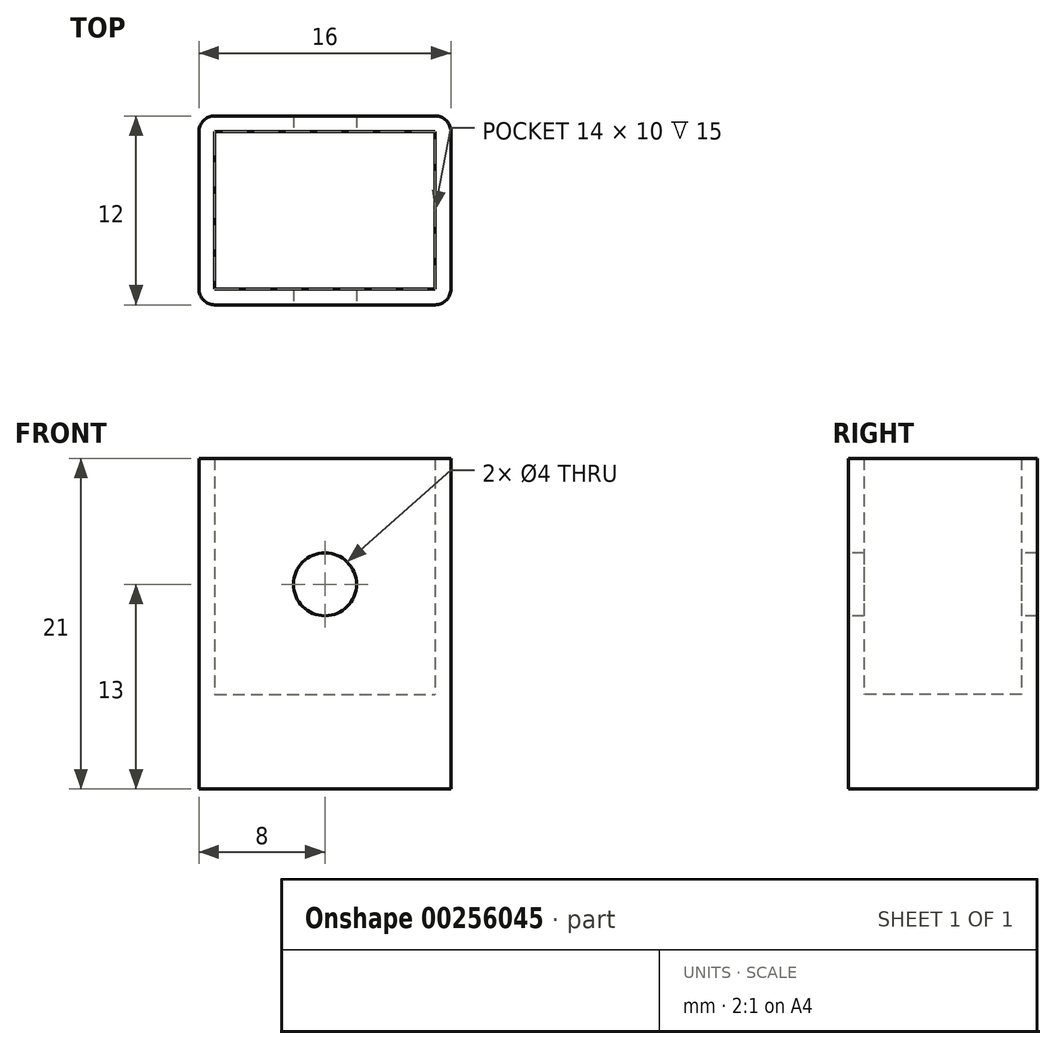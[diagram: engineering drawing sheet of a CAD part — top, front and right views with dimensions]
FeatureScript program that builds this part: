
annotation { "Feature Type Name" : "Feature", "Feature Type Description" : "" }
export const myFeature = defineFeature(function(context is Context, id is Id, definition is map)
    precondition{}
    {
        {
            var Q0;
            Q0=qCreatedBy(makeId("Top.planeOp"),FACE);
            var sketch = newSketch(context, id + "F0", { "sketchPlane" : qUnion([Q0])});
            skLineSegment(sketch, "E0.bottom", {"start": v(-8, 6) * mm, "end": v(8, 6) * mm});
            skLineSegment(sketch, "E0.top", {"start": v(-8, -6) * mm, "end": v(8, -6) * mm});
            skLineSegment(sketch, "E0.left", {"start": v(-8, 6) * mm, "end": v(-8, -6) * mm});
            skLineSegment(sketch, "E0.right", {"start": v(8, 6) * mm, "end": v(8, -6) * mm});
            skLineSegment(sketch, "E1", {"start": v(-8, 6) * mm, "end": v(8, -6) * mm, "construction": true});
            skSolve(sketch);
        }
        {
            var Q0;
            Q0=makeQuery(id+"F0.imprint","IMPRINT",FACE,{"disambiguationData":[TD([[makeQuery(id+"F0.imprint","IMPRINT",EDGE,{"derivedFrom":sQuery(id+"F0.wireOp",EDGE,"E0.bottom")}),-1.0]])]});
            extrude(context, id + "F1", {"entities" : qUnion([Q0]), "depth" : 16 * mm});
        }
        {
            var Q0;
            Q0=makeQuery(id+"F1.opExtrude","CAP_FACE",FACE,{"disambiguationData":[OSD([sQuery(id+"F0.wireOp",EDGE,"E0.bottom"),sQuery(id+"F0.wireOp",EDGE,"E0.top"),sQuery(id+"F0.wireOp",EDGE,"E0.left"),sQuery(id+"F0.wireOp",EDGE,"E0.right")])],"isStart":false});
            shell(context, id + "F2", {"entities" : qUnion([Q0]), "thickness" : 1 * mm});
        }
        {
            var Q0;
            Q0=makeQuery(id+"F1.opExtrude","SWEPT_FACE",FACE,{"disambiguationData":[OSD([sQuery(id+"F0.wireOp",EDGE,"E0.top")])]});
            var sketch = newSketch(context, id + "F3", { "sketchPlane" : qUnion([Q0])});
            skPoint(sketch, "E2", {"position": v(0, 8) * mm});
            skLineSegment(sketch, "E3", {"start": v(-8, 16) * mm, "end": v(8, 0) * mm, "construction": true});
            skSolve(sketch);
        }
        {
            var Q0;
            Q0=sQuery(id+"F3.wireOp",VERTEX,"E2");
            var Q1;
            Q1=makeQuery(id+"F1.opExtrude","SWEPT_BODY",BODY,{"disambiguationData":[OSD([sQuery(id+"F0.wireOp",EDGE,"E0.bottom"),sQuery(id+"F0.wireOp",EDGE,"E0.top"),sQuery(id+"F0.wireOp",EDGE,"E0.left"),sQuery(id+"F0.wireOp",EDGE,"E0.right")])]});
            hole(context, id + "F4", {"style" : HoleStyle.SIMPLE, "endStyle" : HoleEndStyle.THROUGH, "holeDiameter" : 4 * mm, "tappedDepth" : 12.7 * mm, "tapClearance" : 3, "locations" : qUnion([Q0]), "scope" : qUnion([Q1])});
        }
        {
            var Q0;
            Q0=makeQuery(id+"F1.opExtrude","CAP_FACE",FACE,{"disambiguationData":[OSD([sQuery(id+"F0.wireOp",EDGE,"E0.bottom"),sQuery(id+"F0.wireOp",EDGE,"E0.top"),sQuery(id+"F0.wireOp",EDGE,"E0.left"),sQuery(id+"F0.wireOp",EDGE,"E0.right")])],"isStart":true});
            extrude(context, id + "F5", {"entities" : qUnion([Q0]), "operationType" : NewBodyOperationType.ADD, "depth" : 5 * mm});
        }
        {
            var Q0;
            {var subQ0=sQuery(id+"F0.wireOp",EDGE,"E0.right");var subQ1=sQuery(id+"F0.wireOp",EDGE,"E0.top");Q0=makeQuery(id+"F5.boolean.opBoolean","MERGE",EDGE,{"derivedFrom":[makeQuery(id+"F1.opExtrude","SWEPT_EDGE",EDGE,{"disambiguationData":[OSD([subQ1,subQ0])]}),makeQuery(id+"F5.opExtrude","SWEPT_EDGE",EDGE,{"disambiguationData":[OSD([subQ1,subQ0])]})]});}
            var Q1;
            {var subQ0=sQuery(id+"F0.wireOp",EDGE,"E0.left");var subQ1=sQuery(id+"F0.wireOp",EDGE,"E0.top");Q1=makeQuery(id+"F5.boolean.opBoolean","MERGE",EDGE,{"derivedFrom":[makeQuery(id+"F1.opExtrude","SWEPT_EDGE",EDGE,{"disambiguationData":[OSD([subQ1,subQ0])]}),makeQuery(id+"F5.opExtrude","SWEPT_EDGE",EDGE,{"disambiguationData":[OSD([subQ1,subQ0])]})]});}
            var Q2;
            {var subQ0=sQuery(id+"F0.wireOp",EDGE,"E0.right");var subQ1=sQuery(id+"F0.wireOp",EDGE,"E0.bottom");Q2=makeQuery(id+"F5.boolean.opBoolean","MERGE",EDGE,{"derivedFrom":[makeQuery(id+"F1.opExtrude","SWEPT_EDGE",EDGE,{"disambiguationData":[OSD([subQ1,subQ0])]}),makeQuery(id+"F5.opExtrude","SWEPT_EDGE",EDGE,{"disambiguationData":[OSD([subQ1,subQ0])]})]});}
            var Q3;
            {var subQ0=sQuery(id+"F0.wireOp",EDGE,"E0.left");var subQ1=sQuery(id+"F0.wireOp",EDGE,"E0.bottom");Q3=makeQuery(id+"F5.boolean.opBoolean","MERGE",EDGE,{"derivedFrom":[makeQuery(id+"F1.opExtrude","SWEPT_EDGE",EDGE,{"disambiguationData":[OSD([subQ1,subQ0])]}),makeQuery(id+"F5.opExtrude","SWEPT_EDGE",EDGE,{"disambiguationData":[OSD([subQ1,subQ0])]})]});}
            fillet(context, id + "F6", {"entities" : qUnion([Q0, Q1, Q2, Q3]), "radius" : 1 * mm, "tangentPropagation" : true, "allowEdgeOverflow" : false});
        }
    });
